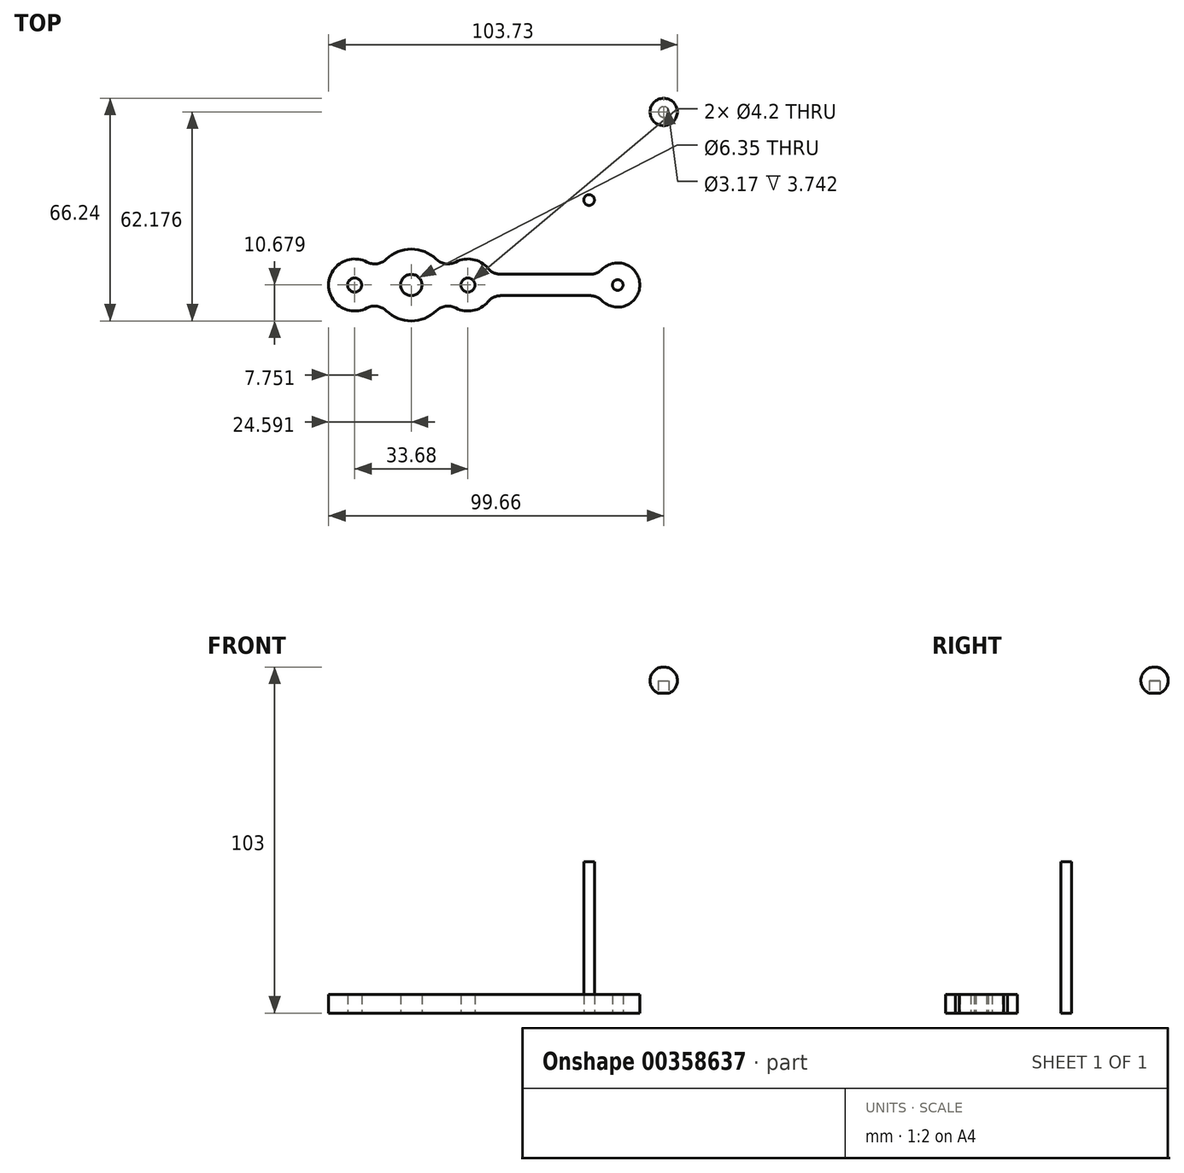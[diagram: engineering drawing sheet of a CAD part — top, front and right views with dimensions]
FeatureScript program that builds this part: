
annotation { "Feature Type Name" : "Feature", "Feature Type Description" : "" }
export const myFeature = defineFeature(function(context is Context, id is Id, definition is map)
    precondition{}
    {
        {
            assignVariable(context, id + "F0", {"name" : "Rod", "anyValue" : 45});
        }
        {
            var Q0;
            Q0=qCreatedBy(makeId("Right.planeOp"),FACE);
            var sketch = newSketch(context, id + "F1", { "sketchPlane" : qUnion([Q0])});
            skArc(sketch, "E0", {"start": v(28.59, 103) * mm, "mid": v(24.6, 99.75) * mm, "end": v(27, 95.2) * mm});
            skLineSegment(sketch, "E1", {"start": v(28.59, 98.94) * mm, "end": v(28.59, 103) * mm});
            skLineSegment(sketch, "E2", {"start": v(28.59, 98.94) * mm, "end": v(27, 98.94) * mm});
            skLineSegment(sketch, "E3", {"start": v(27, 98.94) * mm, "end": v(27, 95.2) * mm});
            skSolve(sketch);
        }
        {
            var Q0;
            Q0=makeQuery(id+"F1.imprint","IMPRINT",FACE,{"disambiguationData":[TD([[makeQuery(id+"F1.imprint","IMPRINT",EDGE,{"derivedFrom":sQuery(id+"F1.wireOp",EDGE,"E0")}),1.0]])]});
            var Q1;
            Q1=sQuery(id+"F1.wireOp",EDGE,"E1");
            revolve(context, id + "F2", {"entities" : qUnion([Q0]), "axis" : qUnion([Q1]), "revolveType" : RevolveType.FULL});
        }
        {
            var Q0;
            Q0=qCreatedBy(makeId("Top.planeOp"),FACE);
            var sketch = newSketch(context, id + "F3", { "sketchPlane" : qUnion([Q0])});
            skCircle(sketch, "E4", {"center": v(-22.19, 2.38) * mm, "radius": 1.59 * mm});
            skSolve(sketch);
        }
        {
            var Q0;
            Q0=makeQuery(id+"F3.imprint","IMPRINT",FACE,{"disambiguationData":[TD([[makeQuery(id+"F3.imprint","IMPRINT",EDGE,{"derivedFrom":sQuery(id+"F3.wireOp",EDGE,"E4")}),1.0]])]});
            extrude(context, id + "F4", {"entities" : qUnion([Q0]), "depth" : (getVariable(context, 'Rod')) * mm, "offsetDistance" : 25 * mm});
        }
        {
            var Q0;
            Q0=qCreatedBy(makeId("Top.planeOp"),FACE);
            var sketch = newSketch(context, id + "F5", { "sketchPlane" : qUnion([Q0])});
            skCircle(sketch, "E5", {"center": v(-75.07, -22.91) * mm, "radius": 3.17 * mm});
            skArc(sketch, "E6", {"start": v(-67.65, -15.23) * mm, "mid": v(-75.07, -12.24) * mm, "end": v(-82.48, -15.23) * mm});
            skCircle(sketch, "E7", {"center": v(-13.69, -22.91) * mm, "radius": 1.59 * mm});
            skLineSegment(sketch, "E8", {"start": v(-75.07, -22.91) * mm, "end": v(-13.69, -22.91) * mm, "construction": true});
            skCircle(sketch, "E9", {"center": v(-58.23, -22.91) * mm, "radius": 2.1 * mm});
            skCircle(sketch, "E10", {"center": v(-58.23, -22.91) * mm, "radius": 2.75 * mm, "construction": true});
            skArc(sketch, "E11", {"start": v(-61.85, -29.76) * mm, "mid": v(-56.73, -30.51) * mm, "end": v(-52.28, -27.88) * mm});
            skArc(sketch, "E12", {"start": v(-67.65, -15.23) * mm, "mid": v(-64.88, -16.59) * mm, "end": v(-61.85, -16.06) * mm});
            skArc(sketch, "E13", {"start": v(-61.85, -29.76) * mm, "mid": v(-64.88, -29.24) * mm, "end": v(-67.65, -30.59) * mm});
            skArc(sketch, "E14", {"start": v(-18.36, -27.56) * mm, "mid": v(-7.1, -22.91) * mm, "end": v(-18.36, -18.26) * mm});
            skLineSegment(sketch, "E15", {"start": v(-75.07, -22.91) * mm, "end": v(-75.07, -6.83) * mm, "construction": true});
            skArc(sketch, "E16.MirrorC", {"start": v(-82.48, -15.23) * mm, "mid": v(-85.25, -16.59) * mm, "end": v(-88.3, -16.06) * mm});
            skArc(sketch, "E17.MirrorC", {"start": v(-88.3, -29.76) * mm, "mid": v(-99.66, -22.91) * mm, "end": v(-88.3, -16.06) * mm});
            skCircle(sketch, "E18.MirrorC", {"center": v(-91.9, -22.91) * mm, "radius": 2.75 * mm, "construction": true});
            skCircle(sketch, "E19.MirrorC", {"center": v(-91.9, -22.91) * mm, "radius": 2.1 * mm});
            skArc(sketch, "E20.MirrorC", {"start": v(-88.3, -29.76) * mm, "mid": v(-85.25, -29.24) * mm, "end": v(-82.48, -30.59) * mm});
            skArc(sketch, "E21", {"start": v(-21.9, -19.74) * mm, "mid": v(-19.98, -19.35) * mm, "end": v(-18.36, -18.26) * mm});
            skArc(sketch, "E22", {"start": v(-18.36, -27.56) * mm, "mid": v(-19.98, -26.47) * mm, "end": v(-21.9, -26.09) * mm});
            skArc(sketch, "E23.trimOffspring", {"start": v(-82.48, -30.59) * mm, "mid": v(-75.07, -33.59) * mm, "end": v(-67.65, -30.59) * mm});
            skArc(sketch, "E24", {"start": v(-52.28, -17.94) * mm, "mid": v(-50.56, -19.27) * mm, "end": v(-48.44, -19.74) * mm});
            skArc(sketch, "E25", {"start": v(-48.44, -26.09) * mm, "mid": v(-50.56, -26.56) * mm, "end": v(-52.28, -27.88) * mm});
            skArc(sketch, "E26.trimOffspring", {"start": v(-52.28, -17.94) * mm, "mid": v(-56.73, -15.3) * mm, "end": v(-61.85, -16.06) * mm});
            skLineSegment(sketch, "E27.trimOffspring", {"start": v(-48.44, -19.74) * mm, "end": v(-21.9, -19.74) * mm});
            skLineSegment(sketch, "E28.trimOffspring", {"start": v(-48.44, -26.09) * mm, "end": v(-21.9, -26.09) * mm});
            skSolve(sketch);
        }
        {
            var Q0;
            Q0=makeQuery(id+"F5.imprint","IMPRINT",FACE,{"disambiguationData":[TD([[makeQuery(id+"F5.imprint","IMPRINT",EDGE,{"derivedFrom":sQuery(id+"F5.wireOp",EDGE,"E5")}),-1.0]])]});
            extrude(context, id + "F6", {"entities" : qUnion([Q0]), "depth" : 5.6 * mm, "offsetDistance" : 25 * mm});
        }
    });
